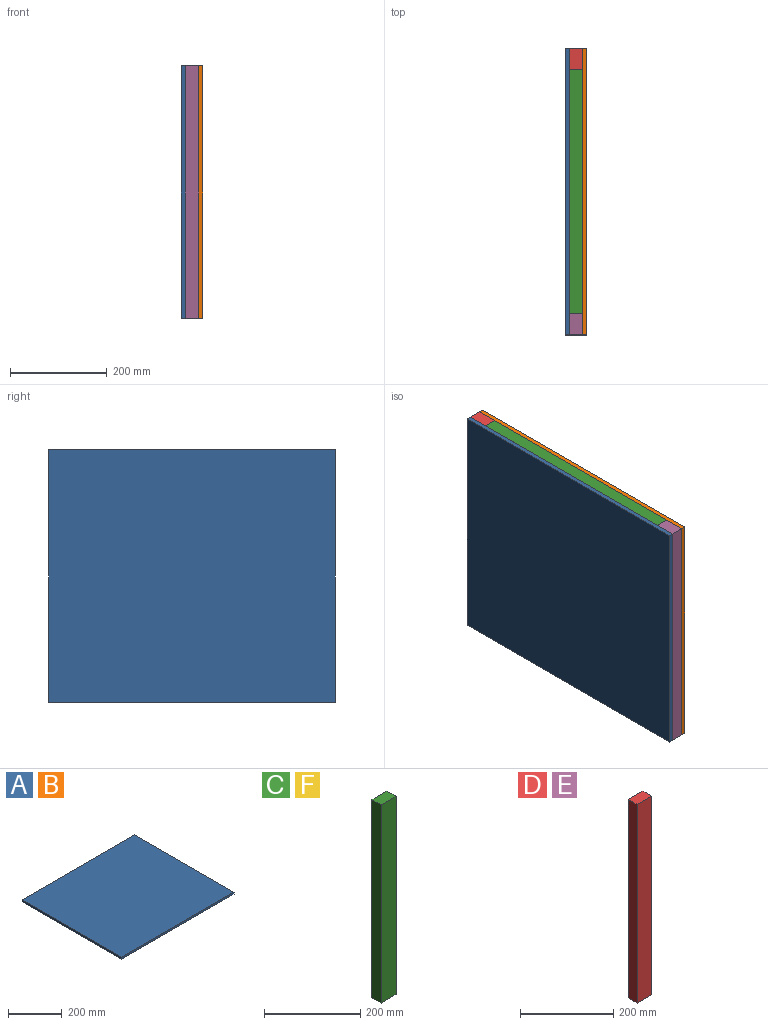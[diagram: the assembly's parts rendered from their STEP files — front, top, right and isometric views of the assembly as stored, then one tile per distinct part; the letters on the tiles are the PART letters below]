
ASSEMBLY  parts=6 mates=5
PART A: 6 faces, bbox 592x522x9 mm
  f0: plane 592x9mm, normal (0,-1,0), area 5328mm2, adj f1,f3,f4,f5
  f1: plane 522x9mm, normal (1,0,0), area 4698mm2, adj f0,f2,f4,f5
  f2: plane 592x9mm, normal (0,1,0), area 5328mm2, adj f1,f3,f4,f5
  f3: plane 522x9mm, normal (-1,0,0), area 4698mm2, adj f0,f2,f4,f5
  f4: plane 592x522mm, normal (0,0,1), area 309024mm2, adj f0,f1,f2,f3
  f5: plane 592x522mm, normal (0,0,-1), area 309024mm2, adj f0,f1,f2,f3
PART B: same geometry as A
PART C: 6 faces, bbox 44x27x504 mm
  f0: plane 504x44mm, normal (0,-1,0), area 22176mm2, adj f1,f3,f4,f5
  f1: plane 504x27mm, normal (1,0,0), area 13608mm2, adj f0,f2,f4,f5
  f2: plane 504x44mm, normal (0,1,0), area 22176mm2, adj f1,f3,f4,f5
  f3: plane 504x27mm, normal (-1,0,0), area 13608mm2, adj f0,f2,f4,f5
  f4: plane 44x27mm, normal (0,0,1), area 1188mm2, adj f0,f1,f2,f3
  f5: plane 44x27mm, normal (0,0,-1), area 1188mm2, adj f0,f1,f2,f3
PART D: 6 faces, bbox 44x27x522 mm
  f0: plane 522x44mm, normal (0,-1,0), area 22968mm2, adj f1,f3,f4,f5
  f1: plane 522x27mm, normal (1,0,0), area 14094mm2, adj f0,f2,f4,f5
  f2: plane 522x44mm, normal (0,1,0), area 22968mm2, adj f1,f3,f4,f5
  f3: plane 522x27mm, normal (-1,0,0), area 14094mm2, adj f0,f2,f4,f5
  f4: plane 44x27mm, normal (0,0,1), area 1188mm2, adj f0,f1,f2,f3
  f5: plane 44x27mm, normal (0,0,-1), area 1188mm2, adj f0,f1,f2,f3
PART E: same geometry as D
PART F: same geometry as C
PLACE A rot(axis=(0.58,-0.58,-0.58),120deg) t=(0,252,261)mm
PLACE B rot(axis=(0.58,-0.58,-0.58),120deg) t=(36,252,261)mm
PLACE C rot(axis=(0.58,0.58,-0.58),120deg) t=(-9.75,504,534.52)mm
PLACE D rot(axis=(0,0,-1),90deg) t=(-17.33,487.29,0)mm
PLACE E rot(axis=(0,0,1),90deg) t=(44.33,16.71,0)mm
PLACE F rot(axis=(0.58,0.58,-0.58),120deg) t=(-9.75,504,56.52)mm
MATE fastened A.f5 <-> F.f0  axis (1,0,0) through (0,252,0)mm
MATE fastened F.f4 <-> E.f1  axis (0,-1,0) through (13.5,0,0)mm
MATE fastened B.f4 <-> F.f2  axis (-1,0,0) through (27,252,0)mm
MATE fastened C.f4 <-> E.f1  axis (0,-1,0) through (13.5,0,522)mm
MATE fastened C.f5 <-> D.f1  axis (0,1,0) through (13.5,504,522)mm
